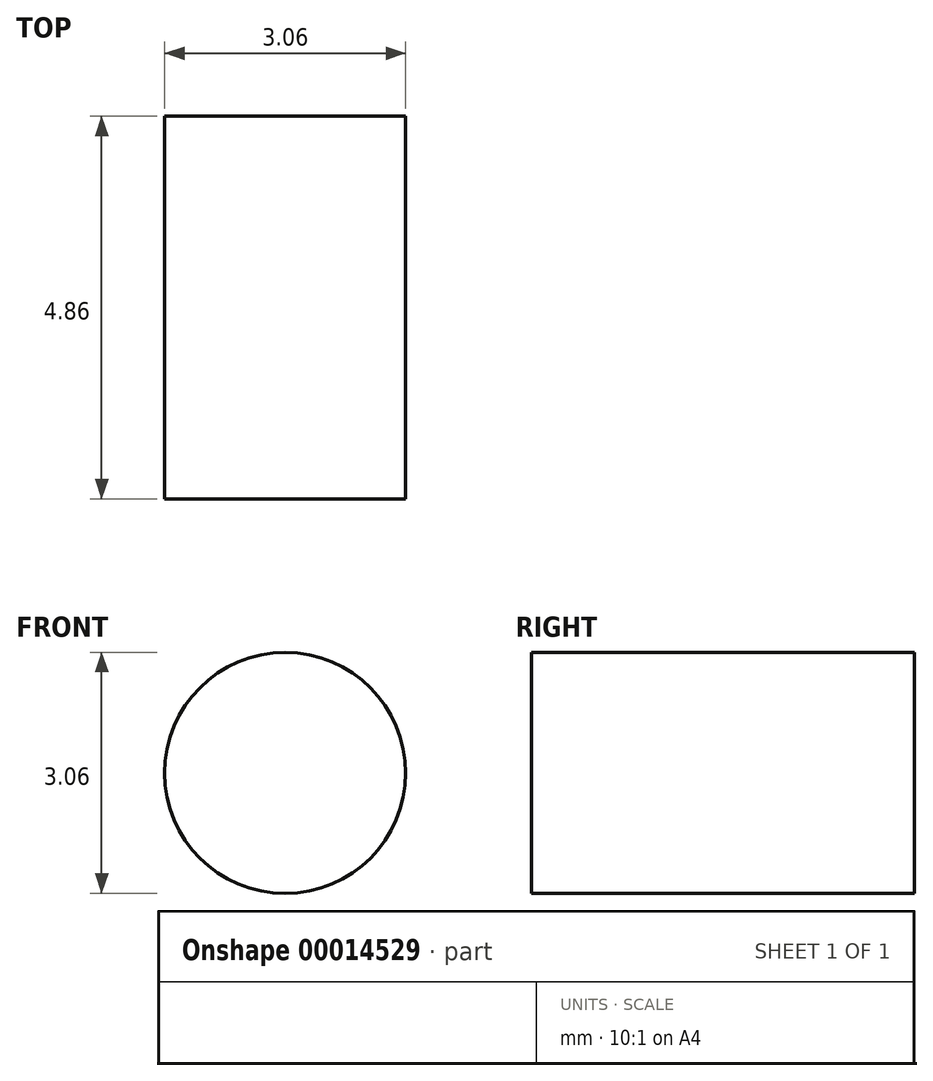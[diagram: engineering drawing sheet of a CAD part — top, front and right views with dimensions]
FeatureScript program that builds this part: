
annotation { "Feature Type Name" : "Feature", "Feature Type Description" : "" }
export const myFeature = defineFeature(function(context is Context, id is Id, definition is map)
    precondition{}
    {
        {
            var Q0;
            Q0=qCreatedBy(makeId("Front.planeOp"),FACE);
            var sketch = newSketch(context, id + "F0", { "sketchPlane" : qUnion([Q0])});
            skCircle(sketch, "E0", {"center": v(-51.77, 41.22) * mm, "radius": 1.53 * mm});
            skSolve(sketch);
        }
        {
            var Q0;
            Q0 = qSketchRegion(id + "F0", true);
            extrude(context, id + "F1", {"entities" : qUnion([Q0]), "depth" : 4.86 * mm});
        }
    });
